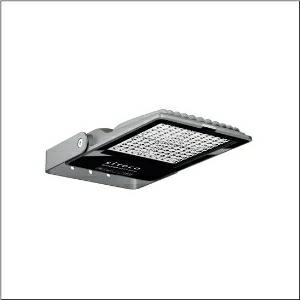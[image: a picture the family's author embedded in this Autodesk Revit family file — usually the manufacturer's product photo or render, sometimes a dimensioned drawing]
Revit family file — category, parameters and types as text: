
# Revit family: sicompact_r__31_mini___pl32_5xa7571f2k23_7a3f
name_source: partatom
category: Lighting Fixtures
units: mm (PartAtom-declared; Revit-internal decimal feet)

## family parameters
Cut with Voids When Loaded = No
Host = Face
Light Source = No
Part Type = Normal
Room Calculation Point = No
Round Connector Dimension = Use Diameter
Shared = No

## types (1)
- SiCompact® 31 mini  PL32 (1 x LED, 20000 lm, 130 W, 4000K)
    Apparent Load = 130 VA
    CIE Flux Codes = 32 69 98 100 100
    Color Rendering = 70
    Color Temperature = 4000K
    Default Elevation = 1800 mm
    Description = SiCompact® 31 mini, floodlight, primary light control with lens, of plastic, of toughened safety glass, transparent, light distribution: PL32, light emission: direct distribution, primary light characteristic: asymmetric, installation type: surface-mounted, LED, High Power LED, rated luminous flux: 20.000lm, luminous efficacy: 154lm/W, light colour: 740, colour temperature: 4000K, control gear: ON/OFF, with cable, 3x 1.5mm², mains connection: 220..240V, AC, 50/60Hz, connection cable pre-assembled, cable length: 2m, rated input power: 130W, of diecast aluminium, specular, metallic grey (RAL 9006), length: 461mm, width: 261mm, height: 62mm, bracket, of sheet steel, coated, metallic grey (RAL 9006), ON/OFF, protection rating (complete): IP66, insulation class (complete): insulation class I (protective earthing), certification: CE, ENEC, impact resistance: IK08, permissible operating ambient temperature: -40..+45°C, packaging unit: 1 piece

Light Distribution: PL32
    Height = 62 mm  [stored 0.203412 ft]
    Lamp = 1 x LED
    Lamp Light Flux = 20000 lm
    Lamp Power = 130 W
    Lamp count = 1
    Length = 460 mm
    Luminous efficacy = 154 lm/W
    Manufacturer = Siteco
    ModVariant = No
    Model = 5XA7571F2K23
    Mounting Place = Wall
    Mounting Type = Surface mounted
    Number of Poles = 1
    OnlyDefault = Yes
    Power Factor = 1
    Product Name = SiCompact® 31 mini | PL32
    Product group = floodlight | wall mounted
    ProductGroupID = 2001
    Protection Class = Protection class I
    Protection Degree = IP 66
    RLX_Detail_Level = 1
    RLX_Emergency_Light_Flux = 0 lm
    RLX_Emergency_Type = 0
    RLX_Emergency_Type_DB = No
    RlxData = <blob elided: 126653 chars, md5=19c17990>
    Socket = socket
    Standby Power = 0 W
    System Light Flux = 20000 lm
    System Power = 130 W
    Type Comments = Product without accessories
    Type Image = l_1006951.jpg
    URL = http://relux.com
    VarID = ---
    Voltage = 0 V
    Weight = 0.00 kg
    Width = 260 mm

note: [stored X ft] marks values corroborated as IEEE doubles in the binary element streams (Revit-internal decimal feet)

## geometry (parser evidence)
native form markers: Blend x4, Sweep x13
no freeform markers — native parametric forms only
